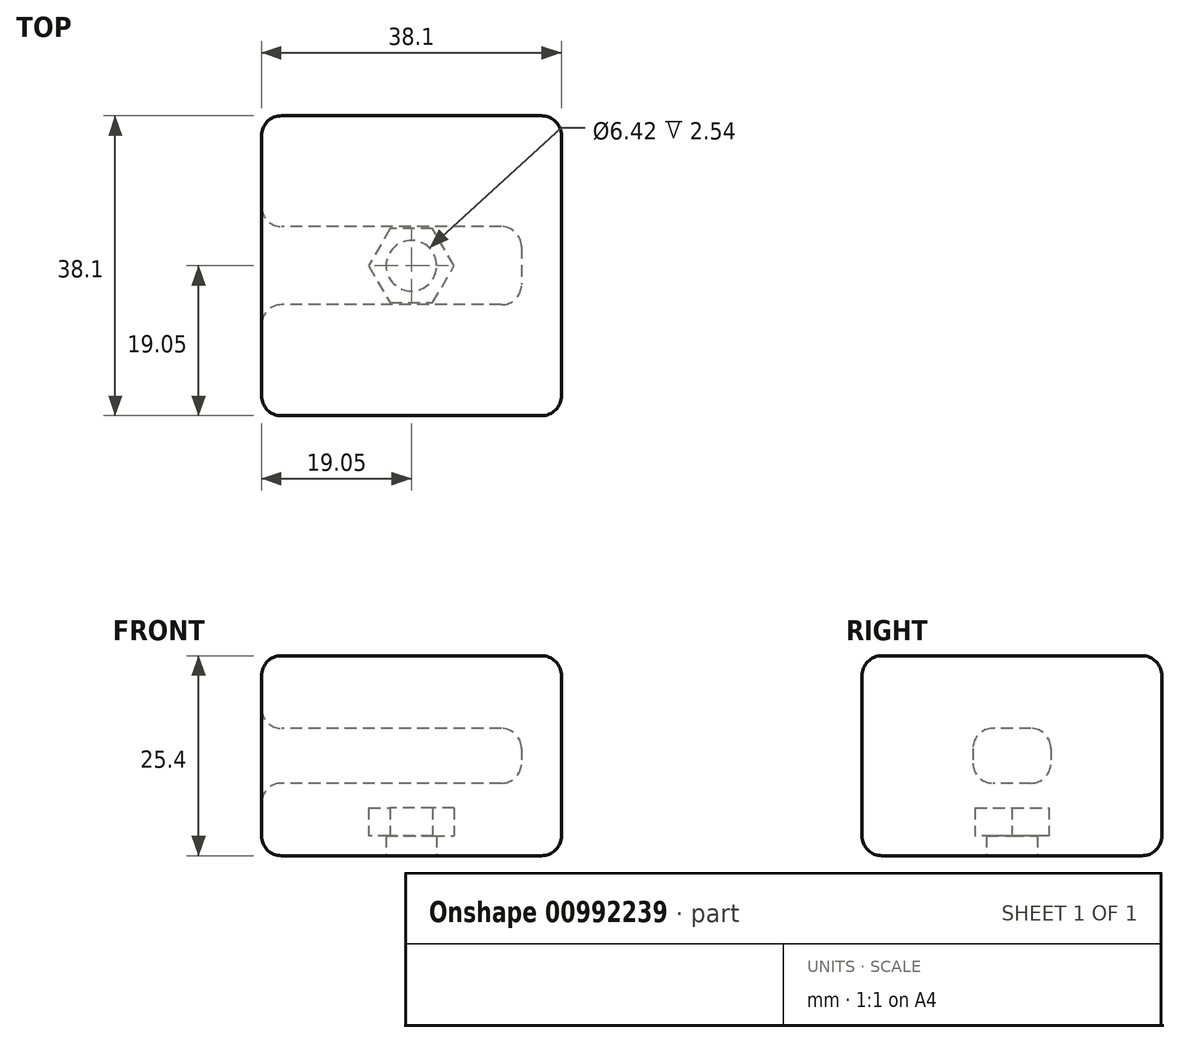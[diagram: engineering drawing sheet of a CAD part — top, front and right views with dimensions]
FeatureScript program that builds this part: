
annotation { "Feature Type Name" : "Feature", "Feature Type Description" : "" }
export const myFeature = defineFeature(function(context is Context, id is Id, definition is map)
    precondition{}
    {
        {
            var Q0;
            Q0=qCreatedBy(makeId("Top.planeOp"),FACE);
            var sketch = newSketch(context, id + "F0", { "sketchPlane" : qUnion([Q0])});
            skLineSegment(sketch, "E0.bottom", {"start": v(19.05, -19.05) * mm, "end": v(-19.05, -19.05) * mm});
            skLineSegment(sketch, "E0.top", {"start": v(19.05, 19.05) * mm, "end": v(-19.05, 19.05) * mm});
            skLineSegment(sketch, "E0.left", {"start": v(19.05, -19.05) * mm, "end": v(19.05, 19.05) * mm});
            skLineSegment(sketch, "E0.right", {"start": v(-19.05, -19.05) * mm, "end": v(-19.05, 19.05) * mm});
            skPoint(sketch, "E0.middle", {"position": v(0, 0) * mm});
            skSolve(sketch);
        }
        {
            var Q0;
            Q0 = qSketchRegion(id + "F0", true);
            extrude(context, id + "F1", {"entities" : qUnion([Q0]), "depth" : 25.4 * mm, "offsetDistance" : 25.4 * mm});
        }
        {
            var Q0;
            Q0=makeQuery(id+"F1.opExtrude","SWEPT_EDGE",EDGE,{"disambiguationData":[OSD([sQuery(id+"F0.wireOp",EDGE,"E0.bottom"),sQuery(id+"F0.wireOp",EDGE,"E0.right")])]});
            var Q1;
            Q1=makeQuery(id+"F1.opExtrude","CAP_EDGE",EDGE,{"disambiguationData":[OSD([sQuery(id+"F0.wireOp",EDGE,"E0.right")])],"isStart":true});
            var Q2;
            Q2=makeQuery(id+"F1.opExtrude","SWEPT_FACE",FACE,{"disambiguationData":[OSD([sQuery(id+"F0.wireOp",EDGE,"E0.bottom")])]});
            var Q3;
            Q3=makeQuery(id+"F1.opExtrude","CAP_FACE",FACE,{"disambiguationData":[OSD([sQuery(id+"F0.wireOp",EDGE,"E0.bottom"),sQuery(id+"F0.wireOp",EDGE,"E0.top"),sQuery(id+"F0.wireOp",EDGE,"E0.left"),sQuery(id+"F0.wireOp",EDGE,"E0.right")])],"isStart":true});
            var Q4;
            Q4=makeQuery(id+"F1.opExtrude","SWEPT_FACE",FACE,{"disambiguationData":[OSD([sQuery(id+"F0.wireOp",EDGE,"E0.right")])]});
            var Q5;
            Q5=makeQuery(id+"F1.opExtrude","CAP_FACE",FACE,{"disambiguationData":[OSD([sQuery(id+"F0.wireOp",EDGE,"E0.bottom"),sQuery(id+"F0.wireOp",EDGE,"E0.top"),sQuery(id+"F0.wireOp",EDGE,"E0.left"),sQuery(id+"F0.wireOp",EDGE,"E0.right")])],"isStart":false});
            var Q6;
            Q6=makeQuery(id+"F1.opExtrude","SWEPT_FACE",FACE,{"disambiguationData":[OSD([sQuery(id+"F0.wireOp",EDGE,"E0.left")])]});
            fillet(context, id + "F2", {"entities" : qUnion([Q0, Q1, Q2, Q3, Q4, Q5, Q6]), "radius" : 2.54 * mm, "tangentPropagation" : true, "allowEdgeOverflow" : false});
        }
        {
            var Q0;
            Q0=makeQuery(id+"F1.opExtrude","SWEPT_FACE",FACE,{"disambiguationData":[OSD([sQuery(id+"F0.wireOp",EDGE,"E0.right")])]});
            var sketch = newSketch(context, id + "F3", { "sketchPlane" : qUnion([Q0])});
            skLineSegment(sketch, "E1.bottom", {"start": v(-4.96, 16.18) * mm, "end": v(4.96, 16.18) * mm});
            skLineSegment(sketch, "E1.top", {"start": v(-4.96, 9.22) * mm, "end": v(4.96, 9.22) * mm});
            skLineSegment(sketch, "E1.left", {"start": v(-4.96, 16.18) * mm, "end": v(-4.96, 9.22) * mm});
            skLineSegment(sketch, "E1.right", {"start": v(4.96, 16.18) * mm, "end": v(4.96, 9.22) * mm});
            skPoint(sketch, "E1.middle", {"position": v(0, 12.7) * mm});
            skLineSegment(sketch, "E2", {"start": v(0, 12.7) * mm, "end": v(0, 0) * mm});
            skLineSegment(sketch, "E3", {"start": v(0, 12.7) * mm, "end": v(0, 25.4) * mm});
            skPoint(sketch, "E3.endSnap0", {"position": v(0, 22.86) * mm});
            skSolve(sketch);
        }
        {
            var Q0;
            {var subQ0=sQuery(id+"F3.wireOp",EDGE,"E1.right");Q0=makeQuery(id+"F3.imprint","IMPRINT",FACE,{"disambiguationData":[TD([[makeQuery(id+"F3.imprint","IMPRINT",EDGE,{"derivedFrom":subQ0}),-1.0]])]});}
            var Q1;
            {var subQ5=sQuery(id+"F3.wireOp",EDGE,"E1.left");Q1=makeQuery(id+"F3.imprint","IMPRINT",FACE,{"disambiguationData":[TD([[makeQuery(id+"F3.imprint","IMPRINT",EDGE,{"derivedFrom":subQ5}),1.0]])]});}
            extrude(context, id + "F4", {"entities" : qUnion([Q0, Q1]), "operationType" : NewBodyOperationType.REMOVE, "oppositeDirection" : true, "depth" : 33.02 * mm, "offsetDistance" : 25.4 * mm});
        }
        {
            var Q0;
            Q0=makeQuery(id+"F1.opExtrude","CAP_FACE",FACE,{"disambiguationData":[OSD([sQuery(id+"F0.wireOp",EDGE,"E0.bottom"),sQuery(id+"F0.wireOp",EDGE,"E0.top"),sQuery(id+"F0.wireOp",EDGE,"E0.left"),sQuery(id+"F0.wireOp",EDGE,"E0.right")])],"isStart":true});
            var sketch = newSketch(context, id + "F5", { "sketchPlane" : qUnion([Q0])});
            skCircle(sketch, "E4.cCircle", {"center": v(0, 0) * mm, "radius": 4.7 * mm, "construction": true});
            skLineSegment(sketch, "E4.0", {"start": v(2.71, -4.7) * mm, "end": v(-2.71, -4.7) * mm});
            skLineSegment(sketch, "E4.1", {"start": v(-2.71, -4.7) * mm, "end": v(-5.43, 0) * mm});
            skLineSegment(sketch, "E4.2", {"start": v(-5.43, 0) * mm, "end": v(-2.71, 4.7) * mm});
            skLineSegment(sketch, "E4.3", {"start": v(-2.71, 4.7) * mm, "end": v(2.71, 4.7) * mm});
            skLineSegment(sketch, "E4.4", {"start": v(2.71, 4.7) * mm, "end": v(5.43, 0) * mm});
            skLineSegment(sketch, "E4.5", {"start": v(5.43, 0) * mm, "end": v(2.71, -4.7) * mm});
            skPoint(sketch, "E4.0.midPoint", {"position": v(0, -4.7) * mm});
            skSolve(sketch);
        }
        {
            var Q0;
            Q0 = qSketchRegion(id + "F5", true);
            extrude(context, id + "F6", {"entities" : qUnion([Q0]), "operationType" : NewBodyOperationType.REMOVE, "oppositeDirection" : true, "depth" : 6.1 * mm, "offsetDistance" : 25.4 * mm});
        }
        {
            var Q0;
            Q0=makeQuery(id+"F5.imprint","IMPRINT",FACE,{"disambiguationData":[TD([[makeQuery(id+"F5.imprint","IMPRINT",EDGE,{"derivedFrom":sQuery(id+"F5.wireOp",EDGE,"E4.0")}),-1.0]])]});
            extrude(context, id + "F7", {"entities" : qUnion([Q0]), "operationType" : NewBodyOperationType.ADD, "oppositeDirection" : true, "depth" : 2.54 * mm, "offsetDistance" : 25.4 * mm});
        }
        {
            var Q0;
            Q0=makeQuery(id+"F4.boolean.opBoolean","COPY",FACE,{"derivedFrom":makeQuery(id+"F4.opExtrude","CAP_FACE",FACE,{"disambiguationData":[OSD([sQuery(id+"F3.wireOp",EDGE,"E1.bottom"),sQuery(id+"F3.wireOp",EDGE,"E1.top"),sQuery(id+"F3.wireOp",EDGE,"E1.left"),sQuery(id+"F3.wireOp",EDGE,"E1.right")])],"isStart":false})});
            var Q1;
            Q1=makeQuery(id+"F4.boolean.opBoolean","COPY",FACE,{"derivedFrom":makeQuery(id+"F4.opExtrude","SWEPT_FACE",FACE,{"disambiguationData":[OSD([sQuery(id+"F3.wireOp",EDGE,"E1.left")])]})});
            var Q2;
            Q2=makeQuery(id+"F4.boolean.opBoolean","COPY",FACE,{"derivedFrom":makeQuery(id+"F4.opExtrude","SWEPT_FACE",FACE,{"disambiguationData":[OSD([sQuery(id+"F3.wireOp",EDGE,"E1.bottom")])]})});
            var Q3;
            Q3=makeQuery(id+"F4.boolean.opBoolean","COPY",FACE,{"derivedFrom":makeQuery(id+"F4.opExtrude","SWEPT_FACE",FACE,{"disambiguationData":[OSD([sQuery(id+"F3.wireOp",EDGE,"E1.right")])]})});
            var Q4;
            Q4=makeQuery(id+"F4.boolean.opBoolean","COPY",FACE,{"derivedFrom":makeQuery(id+"F4.opExtrude","SWEPT_FACE",FACE,{"disambiguationData":[OSD([sQuery(id+"F3.wireOp",EDGE,"E1.top")])]})});
            fillet(context, id + "F8", {"entities" : qUnion([Q0, Q1, Q2, Q3, Q4]), "radius" : 2.54 * mm, "tangentPropagation" : true, "allowEdgeOverflow" : false});
        }
        {
            var Q0;
            Q0=makeQuery(id+"F5.imprint","IMPRINT",FACE,{"disambiguationData":[TD([[makeQuery(id+"F5.imprint","IMPRINT",EDGE,{"derivedFrom":sQuery(id+"F5.wireOp",EDGE,"E4.0")}),-1.0]])]});
            var sketch = newSketch(context, id + "F9", { "sketchPlane" : qUnion([Q0])});
            skCircle(sketch, "E5", {"center": v(0, 0) * mm, "radius": 3.21 * mm});
            skSolve(sketch);
        }
        {
            var Q0;
            Q0 = qSketchRegion(id + "F9", true);
            extrude(context, id + "F10", {"entities" : qUnion([Q0]), "operationType" : NewBodyOperationType.REMOVE, "oppositeDirection" : true, "depth" : 5.08 * mm, "offsetDistance" : 25.4 * mm});
        }
    });
